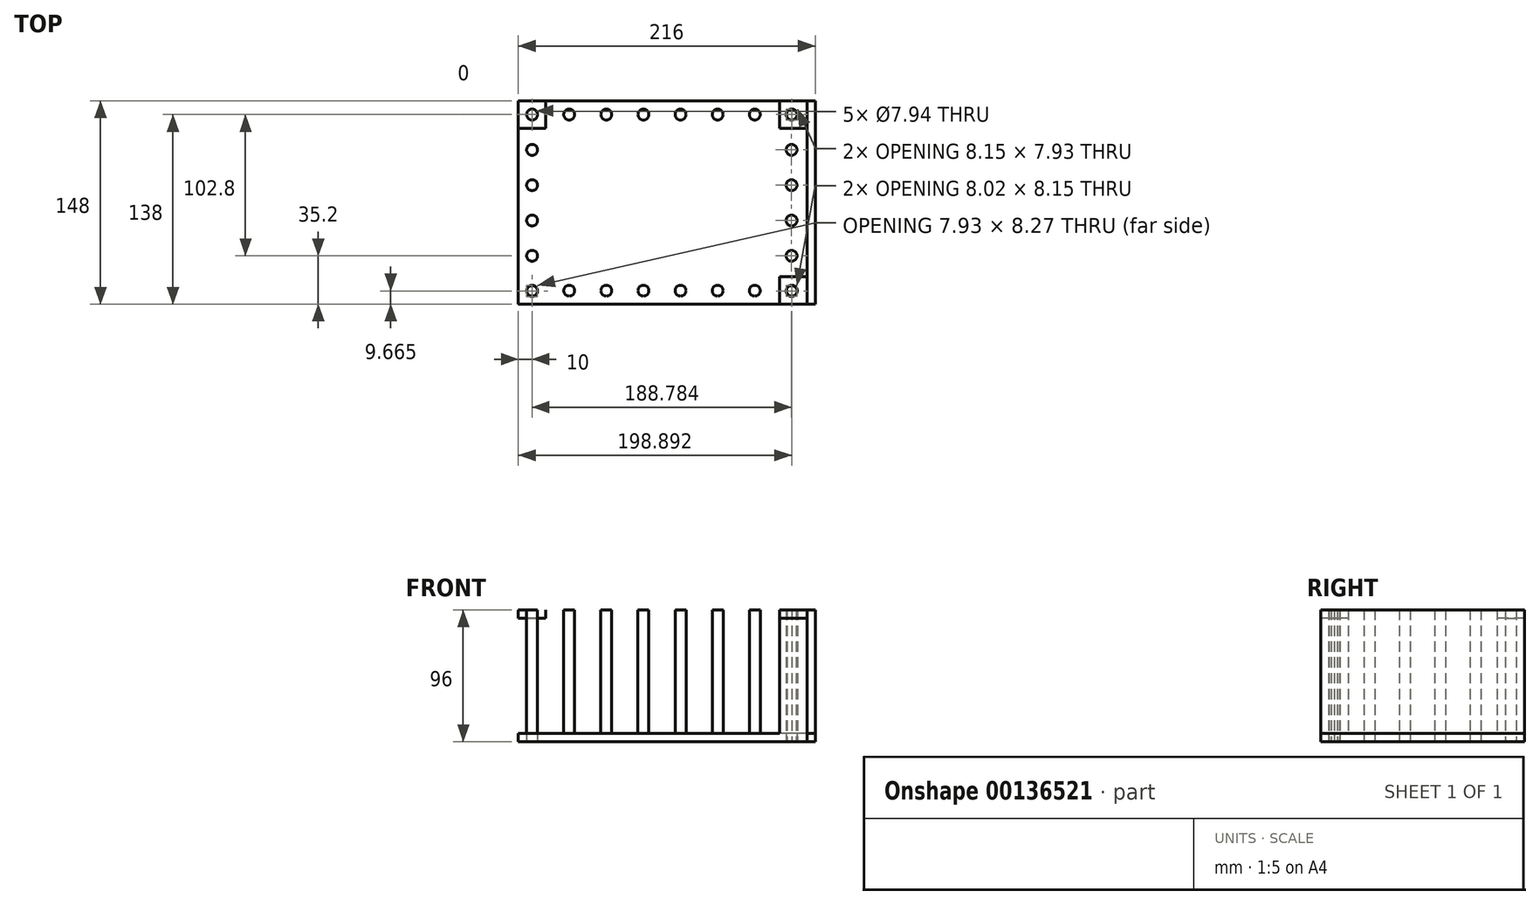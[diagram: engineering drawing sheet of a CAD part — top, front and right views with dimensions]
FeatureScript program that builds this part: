
annotation { "Feature Type Name" : "Feature", "Feature Type Description" : "" }
export const myFeature = defineFeature(function(context is Context, id is Id, definition is map)
    precondition{}
    {
        {
            var Q0;
            Q0=qCreatedBy(makeId("Top.planeOp"),FACE);
            var sketch = newSketch(context, id + "F0", { "sketchPlane" : qUnion([Q0])});
            skLineSegment(sketch, "E0.bottom", {"start": v(0, 0) * mm, "end": v(210, 0) * mm});
            skLineSegment(sketch, "E0.top", {"start": v(0, -148) * mm, "end": v(210, -148) * mm});
            skLineSegment(sketch, "E0.left", {"start": v(0, 0) * mm, "end": v(0, -148) * mm});
            skLineSegment(sketch, "E0.right", {"start": v(210, 0) * mm, "end": v(210, -148) * mm});
            skLineSegment(sketch, "E1.bottom", {"start": v(0, 0) * mm, "end": v(20, 0) * mm});
            skLineSegment(sketch, "E1.top", {"start": v(0, -20) * mm, "end": v(20, -20) * mm});
            skLineSegment(sketch, "E1.left", {"start": v(0, 0) * mm, "end": v(0, -20) * mm});
            skLineSegment(sketch, "E1.right", {"start": v(20, 0) * mm, "end": v(20, -20) * mm});
            skLineSegment(sketch, "E2.0.1.0", {"start": v(0, -128) * mm, "end": v(0, -148) * mm});
            skLineSegment(sketch, "E2.0.1.1", {"start": v(0, -148) * mm, "end": v(20, -148) * mm});
            skLineSegment(sketch, "E2.0.1.2", {"start": v(0, -128) * mm, "end": v(20, -128) * mm});
            skLineSegment(sketch, "E2.0.1.3", {"start": v(20, -128) * mm, "end": v(20, -148) * mm});
            skLineSegment(sketch, "E2.1.0.0", {"start": v(190, 0) * mm, "end": v(190, -20) * mm});
            skLineSegment(sketch, "E2.1.0.1", {"start": v(190, -20) * mm, "end": v(210, -20) * mm});
            skLineSegment(sketch, "E2.1.0.2", {"start": v(190, 0) * mm, "end": v(210, 0) * mm});
            skLineSegment(sketch, "E2.1.0.3", {"start": v(210, 0) * mm, "end": v(210, -20) * mm});
            skLineSegment(sketch, "E2.1.1.0", {"start": v(190, -128) * mm, "end": v(190, -148) * mm});
            skLineSegment(sketch, "E2.1.1.1", {"start": v(190, -148) * mm, "end": v(210, -148) * mm});
            skLineSegment(sketch, "E2.1.1.2", {"start": v(190, -128) * mm, "end": v(210, -128) * mm});
            skLineSegment(sketch, "E2.1.1.3", {"start": v(210, -128) * mm, "end": v(210, -148) * mm});
            skLineSegment(sketch, "E2.direction1", {"start": v(0, 0) * mm, "end": v(190, 0) * mm, "construction": true});
            skLineSegment(sketch, "E2.direction2", {"start": v(0, 0) * mm, "end": v(0, -128) * mm, "construction": true});
            skCircle(sketch, "E3", {"center": v(10, -10) * mm, "radius": 3.97 * mm});
            skPoint(sketch, "E3.centerSnap0", {"position": v(10, -20) * mm});
            skPoint(sketch, "E3.centerSnap1", {"position": v(20, -10) * mm});
            skCircle(sketch, "E4.0.1.0", {"center": v(10, -138.17) * mm, "radius": 3.97 * mm});
            skCircle(sketch, "E4.1.0.0", {"center": v(37, -10) * mm, "radius": 3.97 * mm});
            skCircle(sketch, "E4.1.1.0", {"center": v(37, -138.17) * mm, "radius": 3.97 * mm});
            skCircle(sketch, "E4.2.0.0", {"center": v(64, -10) * mm, "radius": 3.97 * mm});
            skCircle(sketch, "E4.2.1.0", {"center": v(64, -138.17) * mm, "radius": 3.97 * mm});
            skCircle(sketch, "E4.3.0.0", {"center": v(91, -10) * mm, "radius": 3.97 * mm});
            skCircle(sketch, "E4.3.1.0", {"center": v(91, -138.17) * mm, "radius": 3.97 * mm});
            skCircle(sketch, "E4.4.0.0", {"center": v(118, -10) * mm, "radius": 3.97 * mm});
            skCircle(sketch, "E4.4.1.0", {"center": v(118, -138.17) * mm, "radius": 3.97 * mm});
            skCircle(sketch, "E4.5.0.0", {"center": v(145, -10) * mm, "radius": 3.97 * mm});
            skCircle(sketch, "E4.5.1.0", {"center": v(145, -138.17) * mm, "radius": 3.97 * mm});
            skCircle(sketch, "E4.6.0.0", {"center": v(172, -10) * mm, "radius": 3.97 * mm});
            skCircle(sketch, "E4.6.1.0", {"center": v(172, -138.17) * mm, "radius": 3.97 * mm});
            skCircle(sketch, "E4.7.0.0", {"center": v(199, -10) * mm, "radius": 3.97 * mm});
            skCircle(sketch, "E4.7.1.0", {"center": v(199, -138.17) * mm, "radius": 3.97 * mm});
            skLineSegment(sketch, "E4.direction1", {"start": v(10, -10) * mm, "end": v(37, -10) * mm, "construction": true});
            skLineSegment(sketch, "E4.direction2", {"start": v(10, -10) * mm, "end": v(10, -138.17) * mm, "construction": true});
            skCircle(sketch, "E5.0.1.0", {"center": v(10, -35.7) * mm, "radius": 3.97 * mm});
            skCircle(sketch, "E5.0.2.0", {"center": v(10, -61.4) * mm, "radius": 3.97 * mm});
            skCircle(sketch, "E5.0.3.0", {"center": v(10, -87.1) * mm, "radius": 3.97 * mm});
            skCircle(sketch, "E5.0.4.0", {"center": v(10, -112.8) * mm, "radius": 3.97 * mm});
            skCircle(sketch, "E5.0.5.0", {"center": v(10, -138.5) * mm, "radius": 3.97 * mm});
            skCircle(sketch, "E5.1.0.0", {"center": v(198.78, -10) * mm, "radius": 3.97 * mm});
            skCircle(sketch, "E5.1.1.0", {"center": v(198.78, -35.7) * mm, "radius": 3.97 * mm});
            skCircle(sketch, "E5.1.2.0", {"center": v(198.78, -61.4) * mm, "radius": 3.97 * mm});
            skCircle(sketch, "E5.1.3.0", {"center": v(198.78, -87.1) * mm, "radius": 3.97 * mm});
            skCircle(sketch, "E5.1.4.0", {"center": v(198.78, -112.8) * mm, "radius": 3.97 * mm});
            skCircle(sketch, "E5.1.5.0", {"center": v(198.78, -138.5) * mm, "radius": 3.97 * mm});
            skLineSegment(sketch, "E5.direction1", {"start": v(10, -10) * mm, "end": v(198.78, -10) * mm, "construction": true});
            skLineSegment(sketch, "E5.direction2", {"start": v(10, -10) * mm, "end": v(10, -35.7) * mm, "construction": true});
            skLineSegment(sketch, "E6.bottom", {"start": v(210, 0) * mm, "end": v(216, 0) * mm});
            skLineSegment(sketch, "E6.top", {"start": v(210, -148) * mm, "end": v(216, -148) * mm});
            skLineSegment(sketch, "E6.right", {"start": v(216, 0) * mm, "end": v(216, -148) * mm});
            skSolve(sketch);
        }
        {
            var Q0;
            Q0 = qSketchRegion(id + "F0", true);
            extrude(context, id + "F1", {"entities" : qUnion([Q0]), "depth" : 6 * mm});
        }
        {
            var Q0;
            Q0=makeQuery(id+"F0.imprint","IMPRINT",FACE,{"disambiguationData":[TD([[makeQuery(id+"F0.imprint","IMPRINT",EDGE,{"derivedFrom":sQuery(id+"F0.wireOp",EDGE,"E1.bottom")}),-1.0]])]});
            var Q1;
            Q1=makeQuery(id+"F0.imprint","IMPRINT",FACE,{"disambiguationData":[TD([[makeQuery(id+"F0.imprint","IMPRINT",EDGE,{"derivedFrom":sQuery(id+"F0.wireOp",EDGE,"E4.1.0.0")}),1.0]])]});
            var Q2;
            Q2=makeQuery(id+"F0.imprint","IMPRINT",FACE,{"disambiguationData":[TD([[makeQuery(id+"F0.imprint","IMPRINT",EDGE,{"derivedFrom":sQuery(id+"F0.wireOp",EDGE,"E4.2.0.0")}),1.0]])]});
            var Q3;
            Q3=makeQuery(id+"F0.imprint","IMPRINT",FACE,{"disambiguationData":[TD([[makeQuery(id+"F0.imprint","IMPRINT",EDGE,{"derivedFrom":sQuery(id+"F0.wireOp",EDGE,"E4.3.0.0")}),1.0]])]});
            var Q4;
            Q4=makeQuery(id+"F0.imprint","IMPRINT",FACE,{"disambiguationData":[TD([[makeQuery(id+"F0.imprint","IMPRINT",EDGE,{"derivedFrom":sQuery(id+"F0.wireOp",EDGE,"E4.4.0.0")}),1.0]])]});
            var Q5;
            Q5=makeQuery(id+"F0.imprint","IMPRINT",FACE,{"disambiguationData":[TD([[makeQuery(id+"F0.imprint","IMPRINT",EDGE,{"derivedFrom":sQuery(id+"F0.wireOp",EDGE,"E4.5.0.0")}),1.0]])]});
            var Q6;
            Q6=makeQuery(id+"F0.imprint","IMPRINT",FACE,{"disambiguationData":[TD([[makeQuery(id+"F0.imprint","IMPRINT",EDGE,{"derivedFrom":sQuery(id+"F0.wireOp",EDGE,"E4.6.0.0")}),1.0]])]});
            var Q7;
            Q7=makeQuery(id+"F0.imprint","IMPRINT",FACE,{"disambiguationData":[TD([[makeQuery(id+"F0.imprint","IMPRINT",EDGE,{"derivedFrom":sQuery(id+"F0.wireOp",EDGE,"E4.6.1.0")}),1.0]])]});
            var Q8;
            Q8=makeQuery(id+"F0.imprint","IMPRINT",FACE,{"disambiguationData":[TD([[makeQuery(id+"F0.imprint","IMPRINT",EDGE,{"derivedFrom":sQuery(id+"F0.wireOp",EDGE,"E2.1.0.0")}),1.0]])]});
            var Q9;
            Q9=makeQuery(id+"F0.imprint","IMPRINT",FACE,{"disambiguationData":[TD([[makeQuery(id+"F0.imprint","IMPRINT",EDGE,{"derivedFrom":sQuery(id+"F0.wireOp",EDGE,"E2.1.1.0")}),1.0]])]});
            var Q10;
            {var subQ0=sQuery(id+"F0.wireOp",EDGE,"E5.1.5.0");var subQ1=sQuery(id+"F0.wireOp",EDGE,"E4.7.1.0");var subQ2=makeQuery(id+"F0.imprint","INTERSECT",VERTEX,{"disambiguationData":[OD(0.0)],"derivedFrom":[subQ1,subQ0]});Q10=makeQuery(id+"F0.imprint","IMPRINT",FACE,{"disambiguationData":[TD([[makeQuery(id+"F0.imprint","IMPRINT",EDGE,{"disambiguationData":[TD([[subQ2,-1.0]])],"derivedFrom":subQ1}),1.0]])]});}
            var Q11;
            {var subQ0=sQuery(id+"F0.wireOp",EDGE,"E5.1.0.0");var subQ1=sQuery(id+"F0.wireOp",EDGE,"E4.7.0.0");var subQ2=makeQuery(id+"F0.imprint","INTERSECT",VERTEX,{"disambiguationData":[OD(0.0)],"derivedFrom":[subQ1,subQ0]});Q11=makeQuery(id+"F0.imprint","IMPRINT",FACE,{"disambiguationData":[TD([[makeQuery(id+"F0.imprint","IMPRINT",EDGE,{"disambiguationData":[TD([[subQ2,1.0]])],"derivedFrom":subQ1}),1.0]])]});}
            var Q12;
            Q12=makeQuery(id+"F0.imprint","IMPRINT",FACE,{"disambiguationData":[TD([[makeQuery(id+"F0.imprint","IMPRINT",EDGE,{"derivedFrom":sQuery(id+"F0.wireOp",EDGE,"E3")}),1.0]])]});
            var Q13;
            Q13=makeQuery(id+"F0.imprint","IMPRINT",FACE,{"disambiguationData":[TD([[makeQuery(id+"F0.imprint","IMPRINT",EDGE,{"derivedFrom":sQuery(id+"F0.wireOp",EDGE,"E5.0.1.0")}),1.0]])]});
            var Q14;
            Q14=makeQuery(id+"F0.imprint","IMPRINT",FACE,{"disambiguationData":[TD([[makeQuery(id+"F0.imprint","IMPRINT",EDGE,{"derivedFrom":sQuery(id+"F0.wireOp",EDGE,"E5.0.2.0")}),1.0]])]});
            var Q15;
            Q15=makeQuery(id+"F0.imprint","IMPRINT",FACE,{"disambiguationData":[TD([[makeQuery(id+"F0.imprint","IMPRINT",EDGE,{"derivedFrom":sQuery(id+"F0.wireOp",EDGE,"E5.0.3.0")}),1.0]])]});
            var Q16;
            Q16=makeQuery(id+"F0.imprint","IMPRINT",FACE,{"disambiguationData":[TD([[makeQuery(id+"F0.imprint","IMPRINT",EDGE,{"derivedFrom":sQuery(id+"F0.wireOp",EDGE,"E5.0.4.0")}),1.0]])]});
            var Q17;
            Q17=makeQuery(id+"F0.imprint","IMPRINT",FACE,{"disambiguationData":[TD([[makeQuery(id+"F0.imprint","IMPRINT",EDGE,{"derivedFrom":sQuery(id+"F0.wireOp",EDGE,"E2.0.1.0")}),1.0]])]});
            var Q18;
            {var subQ0=sQuery(id+"F0.wireOp",EDGE,"E5.0.5.0");var subQ1=sQuery(id+"F0.wireOp",EDGE,"E4.0.1.0");var subQ2=makeQuery(id+"F0.imprint","INTERSECT",VERTEX,{"disambiguationData":[OD(0.0)],"derivedFrom":[subQ1,subQ0]});Q18=makeQuery(id+"F0.imprint","IMPRINT",FACE,{"disambiguationData":[TD([[makeQuery(id+"F0.imprint","IMPRINT",EDGE,{"disambiguationData":[TD([[subQ2,-1.0]])],"derivedFrom":subQ1}),1.0]])]});}
            var Q19;
            Q19=makeQuery(id+"F0.imprint","IMPRINT",FACE,{"disambiguationData":[TD([[makeQuery(id+"F0.imprint","IMPRINT",EDGE,{"derivedFrom":sQuery(id+"F0.wireOp",EDGE,"E4.1.1.0")}),1.0]])]});
            var Q20;
            Q20=makeQuery(id+"F0.imprint","IMPRINT",FACE,{"disambiguationData":[TD([[makeQuery(id+"F0.imprint","IMPRINT",EDGE,{"derivedFrom":sQuery(id+"F0.wireOp",EDGE,"E4.2.1.0")}),1.0]])]});
            var Q21;
            Q21=makeQuery(id+"F0.imprint","IMPRINT",FACE,{"disambiguationData":[TD([[makeQuery(id+"F0.imprint","IMPRINT",EDGE,{"derivedFrom":sQuery(id+"F0.wireOp",EDGE,"E4.3.1.0")}),1.0]])]});
            var Q22;
            Q22=makeQuery(id+"F0.imprint","IMPRINT",FACE,{"disambiguationData":[TD([[makeQuery(id+"F0.imprint","IMPRINT",EDGE,{"derivedFrom":sQuery(id+"F0.wireOp",EDGE,"E4.4.1.0")}),1.0]])]});
            var Q23;
            Q23=makeQuery(id+"F0.imprint","IMPRINT",FACE,{"disambiguationData":[TD([[makeQuery(id+"F0.imprint","IMPRINT",EDGE,{"derivedFrom":sQuery(id+"F0.wireOp",EDGE,"E4.5.1.0")}),1.0]])]});
            extrude(context, id + "F2", {"entities" : qUnion([Q0, Q1, Q2, Q3, Q4, Q5, Q6, Q7, Q8, Q9, Q10, Q11, Q12, Q13, Q14, Q15, Q16, Q17, Q18, Q19, Q20, Q21, Q22, Q23]), "operationType" : NewBodyOperationType.ADD, "depth" : 96 * mm});
        }
        {
            var Q0;
            {var subQ3=sQuery(id+"F0.wireOp",EDGE,"E6.bottom");Q0=makeQuery(id+"F0.imprint","IMPRINT",FACE,{"disambiguationData":[TD([[makeQuery(id+"F0.imprint","IMPRINT",EDGE,{"derivedFrom":subQ3}),-1.0]])]});}
            extrude(context, id + "F3", {"entities" : qUnion([Q0]), "depth" : 96 * mm});
        }
        {
            var Q0;
            Q0=makeQuery(id+"F0.imprint","IMPRINT",FACE,{"disambiguationData":[TD([[makeQuery(id+"F0.imprint","IMPRINT",EDGE,{"derivedFrom":sQuery(id+"F0.wireOp",EDGE,"E0.bottom")}),-1.0]])]});
            var Q1;
            Q1=makeQuery(id+"F0.imprint","IMPRINT",FACE,{"disambiguationData":[TD([[makeQuery(id+"F0.imprint","IMPRINT",EDGE,{"derivedFrom":sQuery(id+"F0.wireOp",EDGE,"E2.0.1.0")}),1.0]])]});
            var Q2;
            Q2=makeQuery(id+"F0.imprint","IMPRINT",FACE,{"disambiguationData":[TD([[makeQuery(id+"F0.imprint","IMPRINT",EDGE,{"derivedFrom":sQuery(id+"F0.wireOp",EDGE,"E1.bottom")}),-1.0]])]});
            var Q3;
            Q3=makeQuery(id+"F0.imprint","IMPRINT",FACE,{"disambiguationData":[TD([[makeQuery(id+"F0.imprint","IMPRINT",EDGE,{"derivedFrom":sQuery(id+"F0.wireOp",EDGE,"E2.1.0.0")}),1.0]])]});
            var Q4;
            Q4=makeQuery(id+"F0.imprint","IMPRINT",FACE,{"disambiguationData":[TD([[makeQuery(id+"F0.imprint","IMPRINT",EDGE,{"derivedFrom":sQuery(id+"F0.wireOp",EDGE,"E2.1.1.0")}),1.0]])]});
            extrude(context, id + "F4", {"entities" : qUnion([Q0, Q1, Q2, Q3, Q4]), "depth" : 96 * mm, "hasSecondDirection" : true, "secondDirectionOppositeDirection" : false, "secondDirectionDepth" : 90 * mm});
        }
    });
